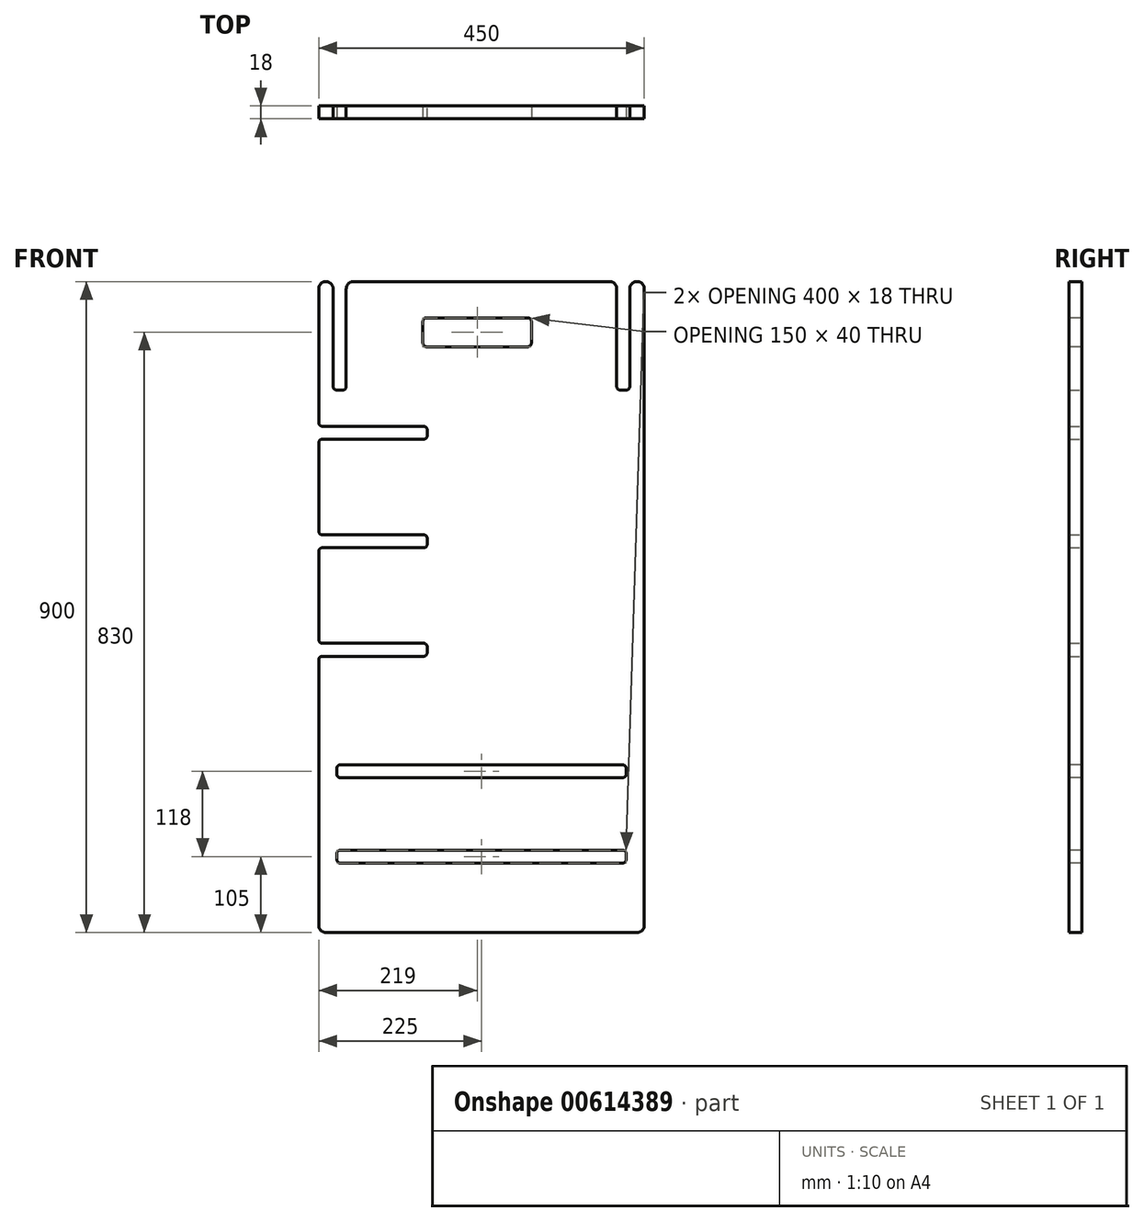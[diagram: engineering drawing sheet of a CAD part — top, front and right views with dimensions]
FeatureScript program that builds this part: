
annotation { "Feature Type Name" : "Feature", "Feature Type Description" : "" }
export const myFeature = defineFeature(function(context is Context, id is Id, definition is map)
    precondition{}
    {
        {
            var Q0;
            Q0=qCreatedBy(makeId("Front.planeOp"),FACE);
            var sketch = newSketch(context, id + "F0", { "sketchPlane" : qUnion([Q0])});
            skLineSegment(sketch, "E0", {"start": v(0, 0) * mm, "end": v(0, 382) * mm});
            skLineSegment(sketch, "E1", {"start": v(0, 382) * mm, "end": v(150, 382) * mm});
            skLineSegment(sketch, "E2", {"start": v(150, 382) * mm, "end": v(150, 400) * mm});
            skLineSegment(sketch, "E3", {"start": v(150, 400) * mm, "end": v(0, 400) * mm});
            skLineSegment(sketch, "E4", {"start": v(0, 400) * mm, "end": v(0, 532) * mm});
            skLineSegment(sketch, "E5", {"start": v(0, 532) * mm, "end": v(150, 532) * mm});
            skLineSegment(sketch, "E6", {"start": v(150, 532) * mm, "end": v(150, 550) * mm});
            skLineSegment(sketch, "E7", {"start": v(150, 550) * mm, "end": v(0, 550) * mm});
            skLineSegment(sketch, "E8", {"start": v(0, 550) * mm, "end": v(0, 682) * mm});
            skLineSegment(sketch, "E9", {"start": v(0, 682) * mm, "end": v(150, 682) * mm});
            skLineSegment(sketch, "E10", {"start": v(150, 682) * mm, "end": v(150, 700) * mm});
            skLineSegment(sketch, "E11", {"start": v(150, 700) * mm, "end": v(0, 700) * mm});
            skLineSegment(sketch, "E12", {"start": v(0, 700) * mm, "end": v(0, 900) * mm});
            skLineSegment(sketch, "E13", {"start": v(0, 900) * mm, "end": v(20, 900) * mm});
            skLineSegment(sketch, "E14", {"start": v(20, 900) * mm, "end": v(20, 750) * mm});
            skLineSegment(sketch, "E15", {"start": v(20, 750) * mm, "end": v(38, 750) * mm});
            skLineSegment(sketch, "E16", {"start": v(38, 750) * mm, "end": v(38, 900) * mm});
            skLineSegment(sketch, "E17", {"start": v(38, 900) * mm, "end": v(412, 900) * mm});
            skLineSegment(sketch, "E18", {"start": v(412, 900) * mm, "end": v(412, 750) * mm});
            skLineSegment(sketch, "E19", {"start": v(412, 750) * mm, "end": v(430, 750) * mm});
            skLineSegment(sketch, "E20", {"start": v(430, 750) * mm, "end": v(430, 900) * mm});
            skLineSegment(sketch, "E21", {"start": v(430, 900) * mm, "end": v(450, 900) * mm});
            skLineSegment(sketch, "E22", {"start": v(450, 900) * mm, "end": v(450, 0) * mm});
            skLineSegment(sketch, "E23", {"start": v(450, 0) * mm, "end": v(0, 0) * mm});
            skSolve(sketch);
        }
        {
            var Q0;
            Q0=makeQuery(id+"F0.imprint","IMPRINT",FACE,{"disambiguationData":[TD([[makeQuery(id+"F0.imprint","IMPRINT",EDGE,{"derivedFrom":sQuery(id+"F0.wireOp",EDGE,"E0")}),-1.0]])]});
            extrude(context, id + "F1", {"entities" : qUnion([Q0]), "depth" : 18 * mm, "offsetDistance" : 25 * mm});
        }
        {
            var Q0;
            Q0=makeQuery(id+"F1.opExtrude","CAP_FACE",FACE,{"disambiguationData":[OSD([sQuery(id+"F0.wireOp",EDGE,"E0"),sQuery(id+"F0.wireOp",EDGE,"E1"),sQuery(id+"F0.wireOp",EDGE,"E2"),sQuery(id+"F0.wireOp",EDGE,"E3"),sQuery(id+"F0.wireOp",EDGE,"E4"),sQuery(id+"F0.wireOp",EDGE,"E5"),sQuery(id+"F0.wireOp",EDGE,"E6"),sQuery(id+"F0.wireOp",EDGE,"E7"),sQuery(id+"F0.wireOp",EDGE,"E8"),sQuery(id+"F0.wireOp",EDGE,"E9"),sQuery(id+"F0.wireOp",EDGE,"E10"),sQuery(id+"F0.wireOp",EDGE,"E11"),sQuery(id+"F0.wireOp",EDGE,"E12"),sQuery(id+"F0.wireOp",EDGE,"E13"),sQuery(id+"F0.wireOp",EDGE,"E14"),sQuery(id+"F0.wireOp",EDGE,"E15"),sQuery(id+"F0.wireOp",EDGE,"E16"),sQuery(id+"F0.wireOp",EDGE,"E17"),sQuery(id+"F0.wireOp",EDGE,"E18"),sQuery(id+"F0.wireOp",EDGE,"E19"),sQuery(id+"F0.wireOp",EDGE,"E20"),sQuery(id+"F0.wireOp",EDGE,"E21"),sQuery(id+"F0.wireOp",EDGE,"E22"),sQuery(id+"F0.wireOp",EDGE,"E23")])],"isStart":false});
            var sketch = newSketch(context, id + "F2", { "sketchPlane" : qUnion([Q0])});
            skLineSegment(sketch, "E24.bottom", {"start": v(25, 232) * mm, "end": v(425, 232) * mm});
            skLineSegment(sketch, "E24.top", {"start": v(25, 214) * mm, "end": v(425, 214) * mm});
            skLineSegment(sketch, "E24.left", {"start": v(25, 232) * mm, "end": v(25, 214) * mm});
            skLineSegment(sketch, "E24.right", {"start": v(425, 232) * mm, "end": v(425, 214) * mm});
            skSolve(sketch);
        }
        {
            var Q0;
            Q0=makeQuery(id+"F2.imprint","IMPRINT",FACE,{"disambiguationData":[TD([[makeQuery(id+"F2.imprint","IMPRINT",EDGE,{"derivedFrom":sQuery(id+"F2.wireOp",EDGE,"E24.bottom")}),-1.0]])]});
            extrude(context, id + "F3", {"entities" : qUnion([Q0]), "operationType" : NewBodyOperationType.REMOVE, "oppositeDirection" : true, "depth" : 25 * mm, "offsetDistance" : 25 * mm});
        }
        {
            var Q0;
            Q0=makeQuery(id+"F1.opExtrude","CAP_FACE",FACE,{"disambiguationData":[OSD([sQuery(id+"F0.wireOp",EDGE,"E0"),sQuery(id+"F0.wireOp",EDGE,"E1"),sQuery(id+"F0.wireOp",EDGE,"E2"),sQuery(id+"F0.wireOp",EDGE,"E3"),sQuery(id+"F0.wireOp",EDGE,"E4"),sQuery(id+"F0.wireOp",EDGE,"E5"),sQuery(id+"F0.wireOp",EDGE,"E6"),sQuery(id+"F0.wireOp",EDGE,"E7"),sQuery(id+"F0.wireOp",EDGE,"E8"),sQuery(id+"F0.wireOp",EDGE,"E9"),sQuery(id+"F0.wireOp",EDGE,"E10"),sQuery(id+"F0.wireOp",EDGE,"E11"),sQuery(id+"F0.wireOp",EDGE,"E12"),sQuery(id+"F0.wireOp",EDGE,"E13"),sQuery(id+"F0.wireOp",EDGE,"E14"),sQuery(id+"F0.wireOp",EDGE,"E15"),sQuery(id+"F0.wireOp",EDGE,"E16"),sQuery(id+"F0.wireOp",EDGE,"E17"),sQuery(id+"F0.wireOp",EDGE,"E18"),sQuery(id+"F0.wireOp",EDGE,"E19"),sQuery(id+"F0.wireOp",EDGE,"E20"),sQuery(id+"F0.wireOp",EDGE,"E21"),sQuery(id+"F0.wireOp",EDGE,"E22"),sQuery(id+"F0.wireOp",EDGE,"E23")])],"isStart":false});
            var sketch = newSketch(context, id + "F4", { "sketchPlane" : qUnion([Q0])});
            skLineSegment(sketch, "E25.bottom", {"start": v(25, 114) * mm, "end": v(425, 114) * mm});
            skLineSegment(sketch, "E25.top", {"start": v(25, 96) * mm, "end": v(425, 96) * mm});
            skLineSegment(sketch, "E25.left", {"start": v(25, 114) * mm, "end": v(25, 96) * mm});
            skLineSegment(sketch, "E25.right", {"start": v(425, 114) * mm, "end": v(425, 96) * mm});
            skSolve(sketch);
        }
        {
            var Q0;
            Q0=makeQuery(id+"F4.imprint","IMPRINT",FACE,{"disambiguationData":[TD([[makeQuery(id+"F4.imprint","IMPRINT",EDGE,{"derivedFrom":sQuery(id+"F4.wireOp",EDGE,"E25.bottom")}),-1.0]])]});
            extrude(context, id + "F5", {"entities" : qUnion([Q0]), "operationType" : NewBodyOperationType.REMOVE, "oppositeDirection" : true, "depth" : 25 * mm, "offsetDistance" : 25 * mm});
        }
        {
            var Q0;
            Q0=makeQuery(id+"F1.opExtrude","SWEPT_EDGE",EDGE,{"disambiguationData":[OSD([sQuery(id+"F0.wireOp",EDGE,"E22"),sQuery(id+"F0.wireOp",EDGE,"E23")])]});
            fillet(context, id + "F6", {"entities" : qUnion([Q0]), "radius" : 10 * mm, "tangentPropagation" : true, "allowEdgeOverflow" : false});
        }
        {
            var Q0;
            Q0=makeQuery(id+"F1.opExtrude","SWEPT_EDGE",EDGE,{"disambiguationData":[OSD([sQuery(id+"F0.wireOp",EDGE,"E0"),sQuery(id+"F0.wireOp",EDGE,"E23")])]});
            fillet(context, id + "F7", {"entities" : qUnion([Q0]), "radius" : 10 * mm, "tangentPropagation" : true, "allowEdgeOverflow" : false});
        }
        {
            var Q0;
            Q0=makeQuery(id+"F1.opExtrude","SWEPT_EDGE",EDGE,{"disambiguationData":[OSD([sQuery(id+"F0.wireOp",EDGE,"E21"),sQuery(id+"F0.wireOp",EDGE,"E22")])]});
            var Q1;
            Q1=makeQuery(id+"F1.opExtrude","SWEPT_EDGE",EDGE,{"disambiguationData":[OSD([sQuery(id+"F0.wireOp",EDGE,"E20"),sQuery(id+"F0.wireOp",EDGE,"E21")])]});
            var Q2;
            Q2=makeQuery(id+"F1.opExtrude","SWEPT_EDGE",EDGE,{"disambiguationData":[OSD([sQuery(id+"F0.wireOp",EDGE,"E17"),sQuery(id+"F0.wireOp",EDGE,"E18")])]});
            var Q3;
            Q3=makeQuery(id+"F1.opExtrude","SWEPT_EDGE",EDGE,{"disambiguationData":[OSD([sQuery(id+"F0.wireOp",EDGE,"E16"),sQuery(id+"F0.wireOp",EDGE,"E17")])]});
            var Q4;
            Q4=makeQuery(id+"F1.opExtrude","SWEPT_EDGE",EDGE,{"disambiguationData":[OSD([sQuery(id+"F0.wireOp",EDGE,"E13"),sQuery(id+"F0.wireOp",EDGE,"E14")])]});
            var Q5;
            Q5=makeQuery(id+"F1.opExtrude","SWEPT_EDGE",EDGE,{"disambiguationData":[OSD([sQuery(id+"F0.wireOp",EDGE,"E12"),sQuery(id+"F0.wireOp",EDGE,"E13")])]});
            fillet(context, id + "F8", {"entities" : qUnion([Q0, Q1, Q2, Q3, Q4, Q5]), "radius" : 10 * mm, "tangentPropagation" : true, "allowEdgeOverflow" : false});
        }
        {
            var Q0;
            Q0=makeQuery(id+"F1.opExtrude","SWEPT_EDGE",EDGE,{"disambiguationData":[OSD([sQuery(id+"F0.wireOp",EDGE,"E0"),sQuery(id+"F0.wireOp",EDGE,"E1")])]});
            var Q1;
            Q1=makeQuery(id+"F1.opExtrude","SWEPT_EDGE",EDGE,{"disambiguationData":[OSD([sQuery(id+"F0.wireOp",EDGE,"E3"),sQuery(id+"F0.wireOp",EDGE,"E4")])]});
            var Q2;
            Q2=makeQuery(id+"F1.opExtrude","SWEPT_EDGE",EDGE,{"disambiguationData":[OSD([sQuery(id+"F0.wireOp",EDGE,"E4"),sQuery(id+"F0.wireOp",EDGE,"E5")])]});
            var Q3;
            Q3=makeQuery(id+"F1.opExtrude","SWEPT_EDGE",EDGE,{"disambiguationData":[OSD([sQuery(id+"F0.wireOp",EDGE,"E7"),sQuery(id+"F0.wireOp",EDGE,"E8")])]});
            var Q4;
            Q4=makeQuery(id+"F1.opExtrude","SWEPT_EDGE",EDGE,{"disambiguationData":[OSD([sQuery(id+"F0.wireOp",EDGE,"E8"),sQuery(id+"F0.wireOp",EDGE,"E9")])]});
            var Q5;
            Q5=makeQuery(id+"F1.opExtrude","SWEPT_EDGE",EDGE,{"disambiguationData":[OSD([sQuery(id+"F0.wireOp",EDGE,"E11"),sQuery(id+"F0.wireOp",EDGE,"E12")])]});
            fillet(context, id + "F9", {"entities" : qUnion([Q0, Q1, Q2, Q3, Q4, Q5]), "radius" : 5 * mm, "tangentPropagation" : true, "allowEdgeOverflow" : false});
        }
        {
            var Q0;
            Q0=makeQuery(id+"F3.boolean.opBoolean","COPY",EDGE,{"derivedFrom":makeQuery(id+"F3.opExtrude","SWEPT_EDGE",EDGE,{"disambiguationData":[OSD([sQuery(id+"F2.wireOp",EDGE,"E24.bottom"),sQuery(id+"F2.wireOp",EDGE,"E24.left")])]})});
            var Q1;
            Q1=makeQuery(id+"F3.boolean.opBoolean","COPY",EDGE,{"derivedFrom":makeQuery(id+"F3.opExtrude","SWEPT_EDGE",EDGE,{"disambiguationData":[OSD([sQuery(id+"F2.wireOp",EDGE,"E24.top"),sQuery(id+"F2.wireOp",EDGE,"E24.left")])]})});
            var Q2;
            Q2=makeQuery(id+"F5.boolean.opBoolean","COPY",EDGE,{"derivedFrom":makeQuery(id+"F5.opExtrude","SWEPT_EDGE",EDGE,{"disambiguationData":[OSD([sQuery(id+"F4.wireOp",EDGE,"E25.top"),sQuery(id+"F4.wireOp",EDGE,"E25.left")])]})});
            var Q3;
            Q3=makeQuery(id+"F5.boolean.opBoolean","COPY",EDGE,{"derivedFrom":makeQuery(id+"F5.opExtrude","SWEPT_EDGE",EDGE,{"disambiguationData":[OSD([sQuery(id+"F4.wireOp",EDGE,"E25.bottom"),sQuery(id+"F4.wireOp",EDGE,"E25.left")])]})});
            var Q4;
            Q4=makeQuery(id+"F5.boolean.opBoolean","COPY",EDGE,{"derivedFrom":makeQuery(id+"F5.opExtrude","SWEPT_EDGE",EDGE,{"disambiguationData":[OSD([sQuery(id+"F4.wireOp",EDGE,"E25.bottom"),sQuery(id+"F4.wireOp",EDGE,"E25.right")])]})});
            var Q5;
            Q5=makeQuery(id+"F5.boolean.opBoolean","COPY",EDGE,{"derivedFrom":makeQuery(id+"F5.opExtrude","SWEPT_EDGE",EDGE,{"disambiguationData":[OSD([sQuery(id+"F4.wireOp",EDGE,"E25.top"),sQuery(id+"F4.wireOp",EDGE,"E25.right")])]})});
            var Q6;
            Q6=makeQuery(id+"F3.boolean.opBoolean","COPY",EDGE,{"derivedFrom":makeQuery(id+"F3.opExtrude","SWEPT_EDGE",EDGE,{"disambiguationData":[OSD([sQuery(id+"F2.wireOp",EDGE,"E24.top"),sQuery(id+"F2.wireOp",EDGE,"E24.right")])]})});
            var Q7;
            Q7=makeQuery(id+"F3.boolean.opBoolean","COPY",EDGE,{"derivedFrom":makeQuery(id+"F3.opExtrude","SWEPT_EDGE",EDGE,{"disambiguationData":[OSD([sQuery(id+"F2.wireOp",EDGE,"E24.bottom"),sQuery(id+"F2.wireOp",EDGE,"E24.right")])]})});
            fillet(context, id + "F10", {"entities" : qUnion([Q0, Q1, Q2, Q3, Q4, Q5, Q6, Q7]), "radius" : 5 * mm, "tangentPropagation" : true, "allowEdgeOverflow" : false});
        }
        {
            var Q0;
            Q0=makeQuery(id+"F1.opExtrude","SWEPT_EDGE",EDGE,{"disambiguationData":[OSD([sQuery(id+"F0.wireOp",EDGE,"E1"),sQuery(id+"F0.wireOp",EDGE,"E2")])]});
            var Q1;
            Q1=makeQuery(id+"F1.opExtrude","SWEPT_EDGE",EDGE,{"disambiguationData":[OSD([sQuery(id+"F0.wireOp",EDGE,"E2"),sQuery(id+"F0.wireOp",EDGE,"E3")])]});
            var Q2;
            Q2=makeQuery(id+"F1.opExtrude","SWEPT_EDGE",EDGE,{"disambiguationData":[OSD([sQuery(id+"F0.wireOp",EDGE,"E5"),sQuery(id+"F0.wireOp",EDGE,"E6")])]});
            var Q3;
            Q3=makeQuery(id+"F1.opExtrude","SWEPT_EDGE",EDGE,{"disambiguationData":[OSD([sQuery(id+"F0.wireOp",EDGE,"E6"),sQuery(id+"F0.wireOp",EDGE,"E7")])]});
            var Q4;
            Q4=makeQuery(id+"F1.opExtrude","SWEPT_EDGE",EDGE,{"disambiguationData":[OSD([sQuery(id+"F0.wireOp",EDGE,"E10"),sQuery(id+"F0.wireOp",EDGE,"E11")])]});
            var Q5;
            Q5=makeQuery(id+"F1.opExtrude","SWEPT_EDGE",EDGE,{"disambiguationData":[OSD([sQuery(id+"F0.wireOp",EDGE,"E9"),sQuery(id+"F0.wireOp",EDGE,"E10")])]});
            var Q6;
            Q6=makeQuery(id+"F1.opExtrude","SWEPT_EDGE",EDGE,{"disambiguationData":[OSD([sQuery(id+"F0.wireOp",EDGE,"E15"),sQuery(id+"F0.wireOp",EDGE,"E16")])]});
            var Q7;
            Q7=makeQuery(id+"F1.opExtrude","SWEPT_EDGE",EDGE,{"disambiguationData":[OSD([sQuery(id+"F0.wireOp",EDGE,"E14"),sQuery(id+"F0.wireOp",EDGE,"E15")])]});
            var Q8;
            Q8=makeQuery(id+"F1.opExtrude","SWEPT_EDGE",EDGE,{"disambiguationData":[OSD([sQuery(id+"F0.wireOp",EDGE,"E18"),sQuery(id+"F0.wireOp",EDGE,"E19")])]});
            var Q9;
            Q9=makeQuery(id+"F1.opExtrude","SWEPT_EDGE",EDGE,{"disambiguationData":[OSD([sQuery(id+"F0.wireOp",EDGE,"E19"),sQuery(id+"F0.wireOp",EDGE,"E20")])]});
            fillet(context, id + "F11", {"entities" : qUnion([Q0, Q1, Q2, Q3, Q4, Q5, Q6, Q7, Q8, Q9]), "radius" : 5 * mm, "tangentPropagation" : true, "allowEdgeOverflow" : false});
        }
        {
            var Q0;
            Q0=makeQuery(id+"F1.opExtrude","CAP_FACE",FACE,{"disambiguationData":[OSD([sQuery(id+"F0.wireOp",EDGE,"E0"),sQuery(id+"F0.wireOp",EDGE,"E1"),sQuery(id+"F0.wireOp",EDGE,"E2"),sQuery(id+"F0.wireOp",EDGE,"E3"),sQuery(id+"F0.wireOp",EDGE,"E4"),sQuery(id+"F0.wireOp",EDGE,"E5"),sQuery(id+"F0.wireOp",EDGE,"E6"),sQuery(id+"F0.wireOp",EDGE,"E7"),sQuery(id+"F0.wireOp",EDGE,"E8"),sQuery(id+"F0.wireOp",EDGE,"E9"),sQuery(id+"F0.wireOp",EDGE,"E10"),sQuery(id+"F0.wireOp",EDGE,"E11"),sQuery(id+"F0.wireOp",EDGE,"E12"),sQuery(id+"F0.wireOp",EDGE,"E13"),sQuery(id+"F0.wireOp",EDGE,"E14"),sQuery(id+"F0.wireOp",EDGE,"E15"),sQuery(id+"F0.wireOp",EDGE,"E16"),sQuery(id+"F0.wireOp",EDGE,"E17"),sQuery(id+"F0.wireOp",EDGE,"E18"),sQuery(id+"F0.wireOp",EDGE,"E19"),sQuery(id+"F0.wireOp",EDGE,"E20"),sQuery(id+"F0.wireOp",EDGE,"E21"),sQuery(id+"F0.wireOp",EDGE,"E22"),sQuery(id+"F0.wireOp",EDGE,"E23")])],"isStart":false});
            var sketch = newSketch(context, id + "F12", { "sketchPlane" : qUnion([Q0])});
            skLineSegment(sketch, "E26.bottom", {"start": v(144, 850) * mm, "end": v(294, 850) * mm});
            skLineSegment(sketch, "E26.top", {"start": v(144, 810) * mm, "end": v(294, 810) * mm});
            skLineSegment(sketch, "E26.left", {"start": v(144, 850) * mm, "end": v(144, 810) * mm});
            skLineSegment(sketch, "E26.right", {"start": v(294, 850) * mm, "end": v(294, 810) * mm});
            skSolve(sketch);
        }
        {
            var Q0;
            Q0 = qSketchRegion(id + "F12", true);
            extrude(context, id + "F13", {"entities" : qUnion([Q0]), "operationType" : NewBodyOperationType.REMOVE, "oppositeDirection" : true, "depth" : 25 * mm, "offsetDistance" : 25 * mm});
        }
        {
            var Q0;
            Q0=makeQuery(id+"F13.boolean.opBoolean","COPY",EDGE,{"derivedFrom":makeQuery(id+"F13.opExtrude","SWEPT_EDGE",EDGE,{"disambiguationData":[OSD([sQuery(id+"F12.wireOp",EDGE,"E26.top"),sQuery(id+"F12.wireOp",EDGE,"E26.left")])]})});
            var Q1;
            Q1=makeQuery(id+"F13.boolean.opBoolean","COPY",EDGE,{"derivedFrom":makeQuery(id+"F13.opExtrude","SWEPT_EDGE",EDGE,{"disambiguationData":[OSD([sQuery(id+"F12.wireOp",EDGE,"E26.bottom"),sQuery(id+"F12.wireOp",EDGE,"E26.left")])]})});
            var Q2;
            Q2=makeQuery(id+"F13.boolean.opBoolean","COPY",EDGE,{"derivedFrom":makeQuery(id+"F13.opExtrude","SWEPT_EDGE",EDGE,{"disambiguationData":[OSD([sQuery(id+"F12.wireOp",EDGE,"E26.bottom"),sQuery(id+"F12.wireOp",EDGE,"E26.right")])]})});
            var Q3;
            Q3=makeQuery(id+"F13.boolean.opBoolean","COPY",EDGE,{"derivedFrom":makeQuery(id+"F13.opExtrude","SWEPT_EDGE",EDGE,{"disambiguationData":[OSD([sQuery(id+"F12.wireOp",EDGE,"E26.top"),sQuery(id+"F12.wireOp",EDGE,"E26.right")])]})});
            fillet(context, id + "F14", {"entities" : qUnion([Q0, Q1, Q2, Q3]), "radius" : 5 * mm, "tangentPropagation" : true, "allowEdgeOverflow" : false});
        }
    });
